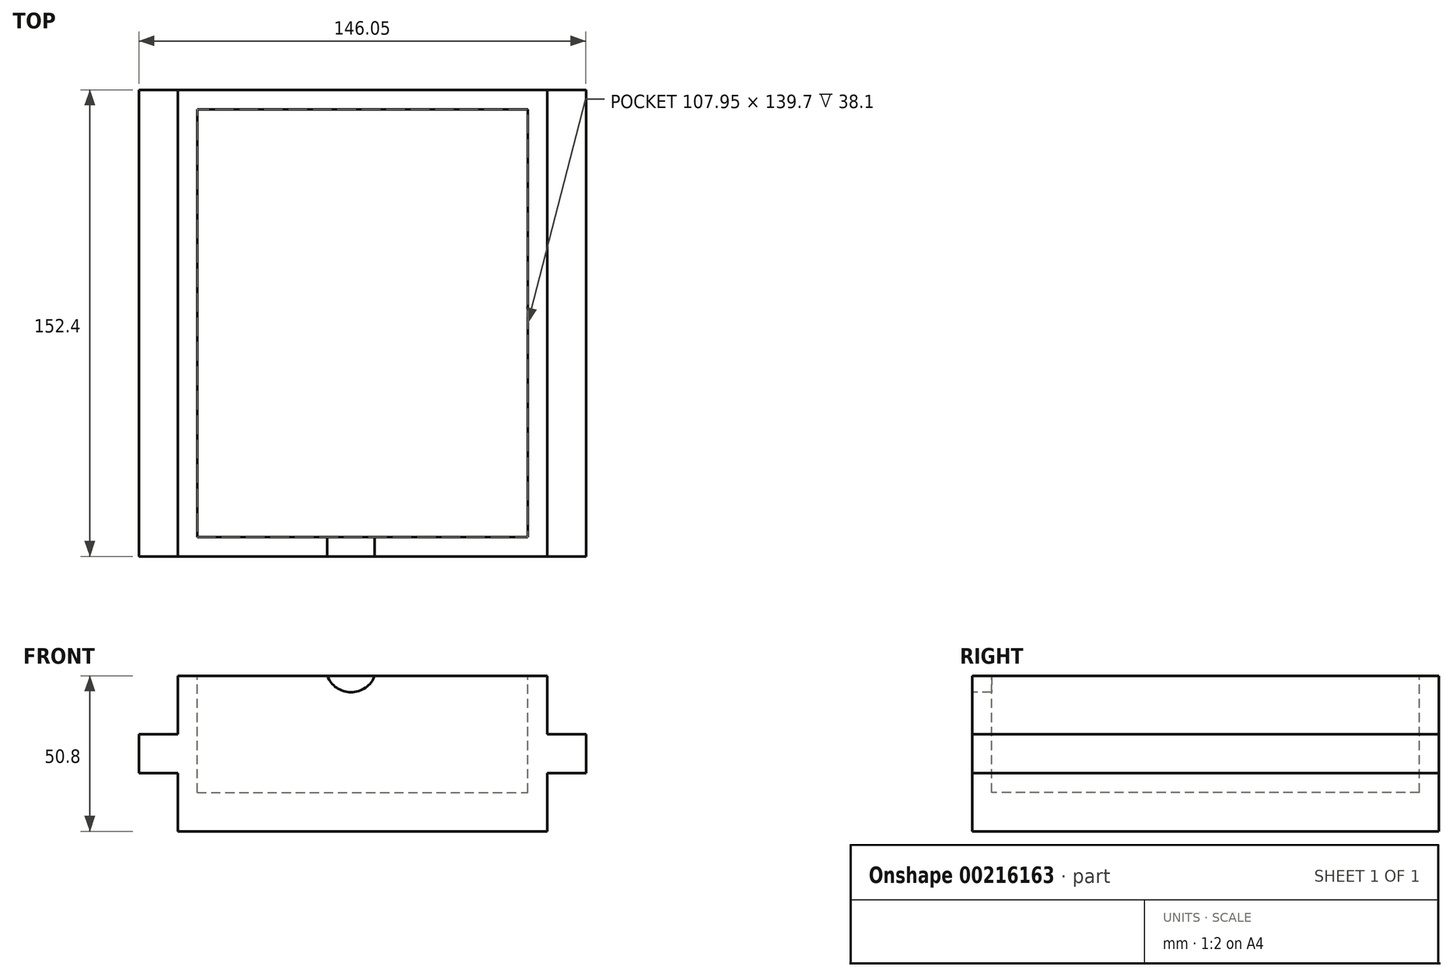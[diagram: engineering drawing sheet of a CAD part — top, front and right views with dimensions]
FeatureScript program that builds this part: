
annotation { "Feature Type Name" : "Feature", "Feature Type Description" : "" }
export const myFeature = defineFeature(function(context is Context, id is Id, definition is map)
    precondition{}
    {
        {
            var Q0;
            Q0=qCreatedBy(makeId("Front.planeOp"),FACE);
            var sketch = newSketch(context, id + "F0", { "sketchPlane" : qUnion([Q0])});
            skLineSegment(sketch, "E0.bottom", {"start": v(-64.36, 19.05) * mm, "end": v(56.3, 19.05) * mm});
            skLineSegment(sketch, "E0.top", {"start": v(-64.36, -31.75) * mm, "end": v(56.3, -31.75) * mm});
            skLineSegment(sketch, "E0.left", {"start": v(-64.36, 19.05) * mm, "end": v(-64.36, -31.75) * mm});
            skLineSegment(sketch, "E0.right", {"start": v(56.3, 19.05) * mm, "end": v(56.3, -31.75) * mm});
            skLineSegment(sketch, "E1.bottom", {"start": v(56.3, 0) * mm, "end": v(69, 0) * mm});
            skLineSegment(sketch, "E1.top", {"start": v(56.3, -12.7) * mm, "end": v(69, -12.7) * mm});
            skLineSegment(sketch, "E1.left", {"start": v(56.3, 0) * mm, "end": v(56.3, -12.7) * mm});
            skLineSegment(sketch, "E1.right", {"start": v(69, 0) * mm, "end": v(69, -12.7) * mm});
            skLineSegment(sketch, "E2.bottom", {"start": v(-64.36, 0) * mm, "end": v(-77.06, 0) * mm});
            skLineSegment(sketch, "E2.top", {"start": v(-64.36, -12.7) * mm, "end": v(-77.06, -12.7) * mm});
            skLineSegment(sketch, "E2.left", {"start": v(-64.36, 0) * mm, "end": v(-64.36, -12.7) * mm});
            skLineSegment(sketch, "E2.right", {"start": v(-77.06, 0) * mm, "end": v(-77.06, -12.7) * mm});
            skSolve(sketch);
        }
        {
            var Q0;
            {var subQ3=sQuery(id+"F0.wireOp",EDGE,"E0.bottom");Q0=makeQuery(id+"F0.imprint","IMPRINT",FACE,{"disambiguationData":[TD([[makeQuery(id+"F0.imprint","IMPRINT",EDGE,{"derivedFrom":subQ3}),-1.0]])]});}
            var Q1;
            Q1=makeQuery(id+"F0.imprint","IMPRINT",FACE,{"disambiguationData":[TD([[makeQuery(id+"F0.imprint","IMPRINT",EDGE,{"derivedFrom":sQuery(id+"F0.wireOp",EDGE,"E2.bottom")}),1.0]])]});
            var Q2;
            Q2=makeQuery(id+"F0.imprint","IMPRINT",FACE,{"disambiguationData":[TD([[makeQuery(id+"F0.imprint","IMPRINT",EDGE,{"derivedFrom":sQuery(id+"F0.wireOp",EDGE,"E1.bottom")}),-1.0]])]});
            extrude(context, id + "F1", {"entities" : qUnion([Q0, Q1, Q2]), "depth" : 152.4 * mm});
        }
        {
            var Q0;
            Q0=makeQuery(id+"F1.opExtrude","SWEPT_FACE",FACE,{"disambiguationData":[OSD([sQuery(id+"F0.wireOp",EDGE,"E0.bottom")])]});
            var sketch = newSketch(context, id + "F2", { "sketchPlane" : qUnion([Q0])});
            skLineSegment(sketch, "E3.bottom", {"start": v(-58, -6.35) * mm, "end": v(49.94, -6.35) * mm});
            skLineSegment(sketch, "E3.top", {"start": v(-58, -146.05) * mm, "end": v(49.94, -146.05) * mm});
            skLineSegment(sketch, "E3.left", {"start": v(-58, -6.35) * mm, "end": v(-58, -146.05) * mm});
            skLineSegment(sketch, "E3.right", {"start": v(49.94, -6.35) * mm, "end": v(49.94, -146.05) * mm});
            skSolve(sketch);
        }
        {
            var Q0;
            Q0=makeQuery(id+"F2.imprint","IMPRINT",FACE,{"disambiguationData":[TD([[makeQuery(id+"F2.imprint","IMPRINT",EDGE,{"derivedFrom":sQuery(id+"F2.wireOp",EDGE,"E3.bottom")}),-1.0]])]});
            extrude(context, id + "F3", {"entities" : qUnion([Q0]), "operationType" : NewBodyOperationType.REMOVE, "oppositeDirection" : true, "depth" : 38.1 * mm});
        }
        {
            var Q0;
            Q0=makeQuery(id+"F1.opExtrude","CAP_FACE",FACE,{"disambiguationData":[OSD([sQuery(id+"F0.wireOp",EDGE,"E0.bottom"),sQuery(id+"F0.wireOp",EDGE,"E0.top"),sQuery(id+"F0.wireOp",EDGE,"E0.left"),sQuery(id+"F0.wireOp",EDGE,"E0.right"),sQuery(id+"F0.wireOp",EDGE,"E1.bottom"),sQuery(id+"F0.wireOp",EDGE,"E1.top"),sQuery(id+"F0.wireOp",EDGE,"E1.right"),sQuery(id+"F0.wireOp",EDGE,"E2.bottom"),sQuery(id+"F0.wireOp",EDGE,"E2.top"),sQuery(id+"F0.wireOp",EDGE,"E2.right")])],"isStart":false});
            var sketch = newSketch(context, id + "F4", { "sketchPlane" : qUnion([Q0])});
            skArc(sketch, "E4", {"start": v(-15.48, 19.05) * mm, "mid": v(-7.74, 13.65) * mm, "end": v(0, 19.05) * mm});
            skSolve(sketch);
        }
        {
            var Q0;
            {var subQ0=sQuery(id+"F4.wireOp",EDGE,"E4");Q0=makeQuery(id+"F4.imprint","IMPRINT",FACE,{"disambiguationData":[TD([[makeQuery(id+"F4.imprint","IMPRINT",EDGE,{"derivedFrom":subQ0}),1.0]])]});}
            extrude(context, id + "F5", {"entities" : qUnion([Q0]), "operationType" : NewBodyOperationType.REMOVE, "oppositeDirection" : true, "depth" : 6.35 * mm});
        }
    });
